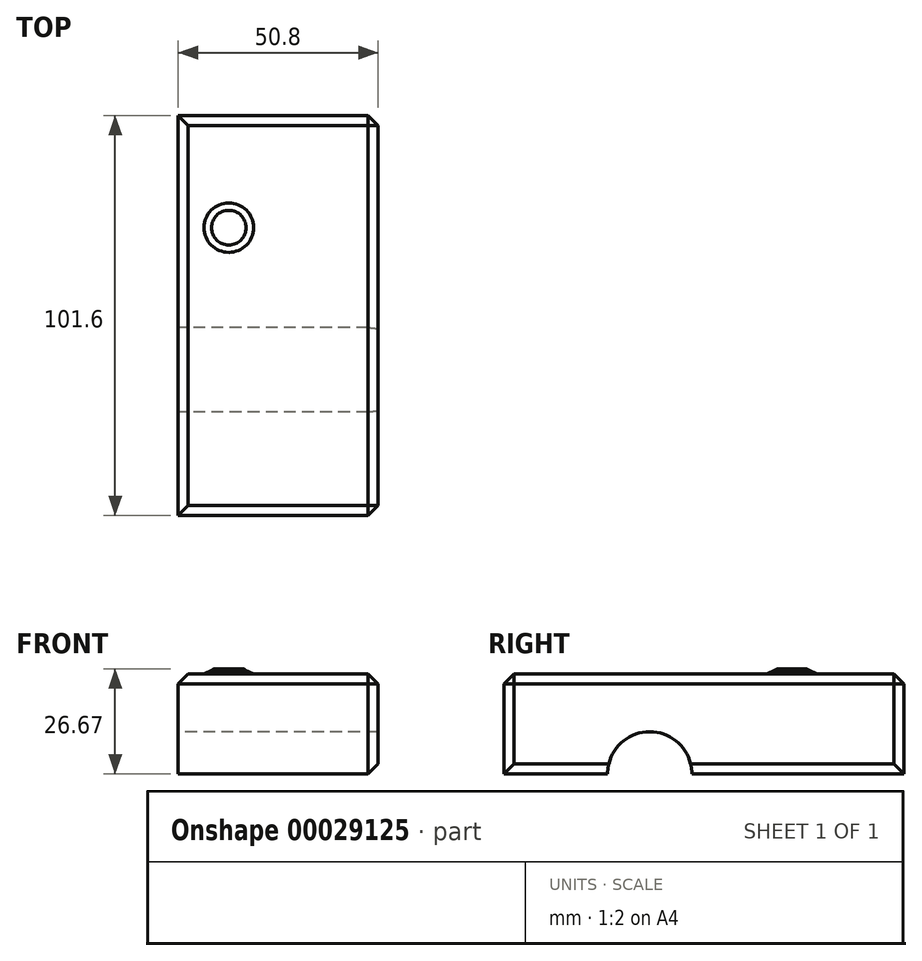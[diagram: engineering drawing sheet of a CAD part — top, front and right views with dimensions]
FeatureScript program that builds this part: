
annotation { "Feature Type Name" : "Feature", "Feature Type Description" : "" }
export const myFeature = defineFeature(function(context is Context, id is Id, definition is map)
    precondition{}
    {
        {
            var Q0;
            Q0=qCreatedBy(makeId("Top.planeOp"),FACE);
            var sketch = newSketch(context, id + "F0", { "sketchPlane" : qUnion([Q0])});
            skLineSegment(sketch, "E0.bottom", {"start": v(-25.4, 50.8) * mm, "end": v(25.4, 50.8) * mm});
            skLineSegment(sketch, "E0.top", {"start": v(-25.4, -50.8) * mm, "end": v(25.4, -50.8) * mm});
            skLineSegment(sketch, "E0.left", {"start": v(-25.4, 50.8) * mm, "end": v(-25.4, -50.8) * mm});
            skLineSegment(sketch, "E0.right", {"start": v(25.4, 50.8) * mm, "end": v(25.4, -50.8) * mm});
            skSolve(sketch);
        }
        {
            var Q0;
            Q0 = qSketchRegion(id + "F0", true);
            extrude(context, id + "F1", {"entities" : qUnion([Q0]), "depth" : 25.4 * mm});
        }
        {
            var Q0;
            Q0=makeQuery(id+"F1.opExtrude","CAP_FACE",FACE,{"disambiguationData":[OSD([sQuery(id+"F0.wireOp",EDGE,"E0.bottom"),sQuery(id+"F0.wireOp",EDGE,"E0.top"),sQuery(id+"F0.wireOp",EDGE,"E0.left"),sQuery(id+"F0.wireOp",EDGE,"E0.right")])],"isStart":false});
            var sketch = newSketch(context, id + "F2", { "sketchPlane" : qUnion([Q0])});
            skCircle(sketch, "E1", {"center": v(-12.54, 22.33) * mm, "radius": 4.72 * mm});
            skSolve(sketch);
        }
        {
            var Q0;
            Q0 = qSketchRegion(id + "F2", true);
            extrude(context, id + "F3", {"entities" : qUnion([Q0]), "operationType" : NewBodyOperationType.ADD, "depth" : 1.27 * mm});
        }
        {
            var Q0;
            Q0=makeQuery(id+"F3.opExtrude","CAP_FACE",FACE,{"disambiguationData":[OSD([sQuery(id+"F2.wireOp",EDGE,"E1")])],"isStart":false});
            fillet(context, id + "F4", {"entities" : qUnion([Q0]), "radius" : 1.27 * mm, "tangentPropagation" : true, "allowEdgeOverflow" : false});
        }
        {
            var Q0;
            Q0=makeQuery(id+"F1.opExtrude","CAP_FACE",FACE,{"disambiguationData":[OSD([sQuery(id+"F0.wireOp",EDGE,"E0.bottom"),sQuery(id+"F0.wireOp",EDGE,"E0.top"),sQuery(id+"F0.wireOp",EDGE,"E0.left"),sQuery(id+"F0.wireOp",EDGE,"E0.right")])],"isStart":false});
            var Q1;
            Q1=makeQuery(id+"F1.opExtrude","SWEPT_FACE",FACE,{"disambiguationData":[OSD([sQuery(id+"F0.wireOp",EDGE,"E0.right")])]});
            chamfer(context, id + "F5", {"entities" : qUnion([Q0, Q1]), "width" : 2.54 * mm, "tangentPropagation" : true});
        }
        {
            var Q0;
            Q0=makeQuery(id+"F1.opExtrude","SWEPT_FACE",FACE,{"disambiguationData":[OSD([sQuery(id+"F0.wireOp",EDGE,"E0.right")])]});
            var sketch = newSketch(context, id + "F6", { "sketchPlane" : qUnion([Q0])});
            skCircle(sketch, "E2", {"center": v(-13.8, 0) * mm, "radius": 10.7 * mm});
            skSolve(sketch);
        }
        {
            var Q0;
            {var subQ0=sQuery(id+"F0.wireOp",EDGE,"E0.right");var subQ1=makeQuery(id+"F5.opChamfer","BLEND_EDGE",EDGE,{"blendedFrom":[makeQuery(id+"F1.opExtrude","CAP_EDGE",EDGE,{"disambiguationData":[OSD([subQ0])],"isStart":true}),makeQuery(id+"F1.opExtrude","SWEPT_FACE",FACE,{"disambiguationData":[OSD([subQ0])]})],"blendedInto":[makeQuery(id+"F1.opExtrude","SWEPT_FACE",FACE,{"disambiguationData":[OSD([subQ0])]})]});var subQ2=sQuery(id+"F6.wireOp",EDGE,"E2");var subQ4=makeQuery(id+"F6.imprint","INTERSECT",VERTEX,{"disambiguationData":[OD(0.0)],"derivedFrom":[subQ1,subQ2]});Q0=makeQuery(id+"F6.imprint","IMPRINT",FACE,{"disambiguationData":[TD([[makeQuery(id+"F6.imprint","IMPRINT",EDGE,{"disambiguationData":[TD([[subQ4,-1.0]])],"derivedFrom":subQ2}),1.0]])]});}
            var Q1;
            {var subQ0=sQuery(id+"F0.wireOp",EDGE,"E0.right");var subQ1=makeQuery(id+"F5.opChamfer","BLEND_EDGE",EDGE,{"blendedFrom":[makeQuery(id+"F1.opExtrude","CAP_EDGE",EDGE,{"disambiguationData":[OSD([subQ0])],"isStart":true}),makeQuery(id+"F1.opExtrude","SWEPT_FACE",FACE,{"disambiguationData":[OSD([subQ0])]})],"blendedInto":[makeQuery(id+"F1.opExtrude","SWEPT_FACE",FACE,{"disambiguationData":[OSD([subQ0])]})]});var subQ2=sQuery(id+"F6.wireOp",EDGE,"E2");var subQ4=makeQuery(id+"F6.imprint","INTERSECT",VERTEX,{"disambiguationData":[OD(0.0)],"derivedFrom":[subQ1,subQ2]});Q1=makeQuery(id+"F6.imprint","IMPRINT",FACE,{"disambiguationData":[TD([[makeQuery(id+"F6.imprint","IMPRINT",EDGE,{"disambiguationData":[TD([[subQ4,1.0]])],"derivedFrom":subQ2}),1.0]])]});}
            var Q2;
            Q2=sQuery(id+"F6.wireOp",EDGE,"E2");
            extrude(context, id + "F7", {"entities" : qUnion([Q0, Q1]), "operationType" : NewBodyOperationType.REMOVE, "surfaceEntities" : qUnion([Q2]), "depth" : 25.4 * mm, "hasSecondDirection" : true, "secondDirectionOppositeDirection" : true, "secondDirectionDepth" : 72.6 * mm});
        }
    });
